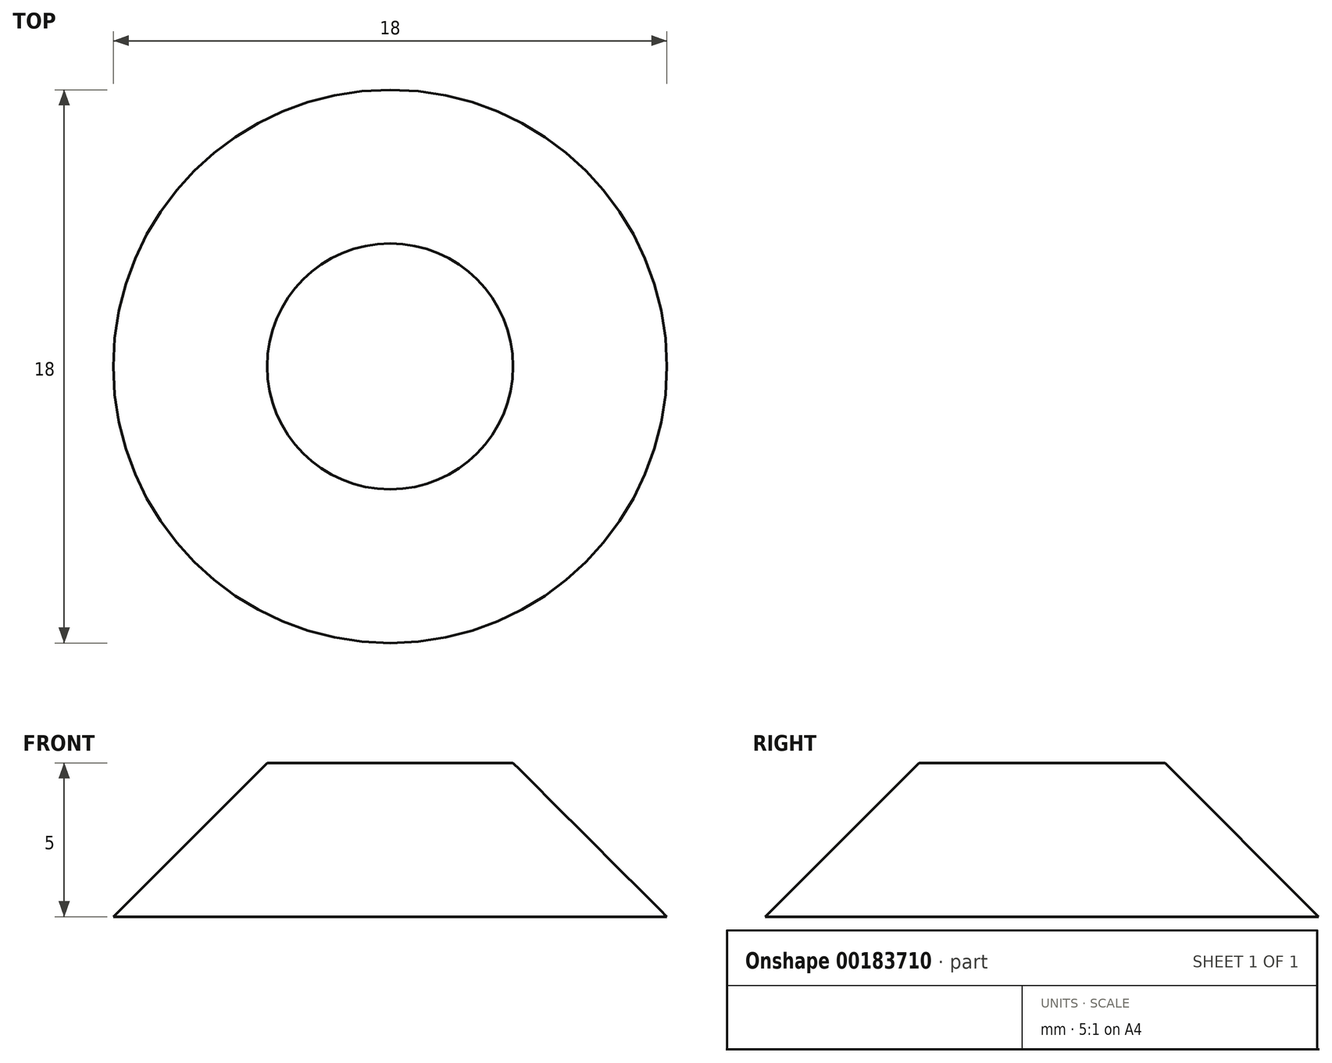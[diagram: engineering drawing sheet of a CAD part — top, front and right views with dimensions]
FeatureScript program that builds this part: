
annotation { "Feature Type Name" : "Feature", "Feature Type Description" : "" }
export const myFeature = defineFeature(function(context is Context, id is Id, definition is map)
    precondition{}
    {
        {
            var Q0;
            Q0=qCreatedBy(makeId("Front.planeOp"),FACE);
            var sketch = newSketch(context, id + "F0", { "sketchPlane" : qUnion([Q0])});
            skLineSegment(sketch, "E0", {"start": v(0, 0) * mm, "end": v(0, 54) * mm});
            skLineSegment(sketch, "E1", {"start": v(0, 37) * mm, "end": v(17, 37) * mm});
            skLineSegment(sketch, "E2", {"start": v(17, 37) * mm, "end": v(-17, 37) * mm});
            skLineSegment(sketch, "E3", {"start": v(0, 54) * mm, "end": v(-17, 37) * mm});
            skLineSegment(sketch, "E4", {"start": v(-17, 37) * mm, "end": v(0, 0) * mm});
            skLineSegment(sketch, "E5", {"start": v(0, 0) * mm, "end": v(17, 37) * mm});
            skLineSegment(sketch, "E6", {"start": v(17, 37) * mm, "end": v(0, 54) * mm});
            skSolve(sketch);
        }
        {
            var Q0;
            Q0=qCreatedBy(makeId("Right.planeOp"),FACE);
            var sketch = newSketch(context, id + "F1", { "sketchPlane" : qUnion([Q0])});
            skLineSegment(sketch, "E7", {"start": v(0, 0) * mm, "end": v(0, 37) * mm});
            skLineSegment(sketch, "E8", {"start": v(0, 37) * mm, "end": v(-10, 37) * mm});
            skLineSegment(sketch, "E9", {"start": v(0, 37) * mm, "end": v(10, 37) * mm});
            skLineSegment(sketch, "E10", {"start": v(0, 54.14) * mm, "end": v(10, 37) * mm});
            skLineSegment(sketch, "E11", {"start": v(0, 54.14) * mm, "end": v(-10, 37) * mm});
            skLineSegment(sketch, "E12", {"start": v(-10, 37) * mm, "end": v(0, 0) * mm});
            skLineSegment(sketch, "E13", {"start": v(10, 37) * mm, "end": v(0, 0) * mm});
            skSolve(sketch);
        }
        {
            var Q0;
            Q0=qCreatedBy(makeId("Top.planeOp"),FACE);
            var sketch = newSketch(context, id + "F2", { "sketchPlane" : qUnion([Q0])});
            skCircle(sketch, "E14", {"center": v(0, 0) * mm, "radius": 9 * mm});
            skSolve(sketch);
        }
        {
            var Q0;
            Q0=makeQuery(id+"F2.imprint","IMPRINT",FACE,{"disambiguationData":[TD([[makeQuery(id+"F2.imprint","IMPRINT",EDGE,{"derivedFrom":sQuery(id+"F2.wireOp",EDGE,"E14")}),1.0]])]});
            extrude(context, id + "F3", {"entities" : qUnion([Q0]), "depth" : 5 * mm});
        }
        {
            var Q0;
            Q0=makeQuery(id+"F3.opExtrude","CAP_FACE",FACE,{"disambiguationData":[OSD([sQuery(id+"F2.wireOp",EDGE,"E14")])],"isStart":false});
            chamfer(context, id + "F4", {"entities" : qUnion([Q0]), "width" : 5 * mm, "tangentPropagation" : true});
        }
        {
            var Q0;
            Q0=sQuery(id+"F0.wireOp",EDGE,"E6");
            var Q1;
            Q1=sQuery(id+"F1.wireOp",EDGE,"E11");
            loft(context, id + "F5", {"bodyType" : ToolBodyType.SURFACE, "wireProfilesArray" : [{ "wireProfileEntities" : qUnion([Q0]) }, { "wireProfileEntities" : qUnion([Q1]) }]});
        }
        {
            var Q0;
            Q0=sQuery(id+"F0.wireOp",EDGE,"E6");
            var Q1;
            Q1=sQuery(id+"F1.wireOp",EDGE,"E10");
            loft(context, id + "F6", {"bodyType" : ToolBodyType.SURFACE, "wireProfilesArray" : [{ "wireProfileEntities" : qUnion([Q0]) }, { "wireProfileEntities" : qUnion([Q1]) }]});
        }
        {
            var Q0;
            Q0=sQuery(id+"F1.wireOp",EDGE,"E11");
            var Q1;
            Q1=sQuery(id+"F0.wireOp",EDGE,"E3");
            loft(context, id + "F7", {"bodyType" : ToolBodyType.SURFACE, "wireProfilesArray" : [{ "wireProfileEntities" : qUnion([Q0]) }, { "wireProfileEntities" : qUnion([Q1]) }]});
        }
        {
            var Q0;
            Q0=sQuery(id+"F1.wireOp",EDGE,"E10");
            var Q1;
            Q1=sQuery(id+"F0.wireOp",EDGE,"E3");
            loft(context, id + "F8", {"bodyType" : ToolBodyType.SURFACE, "wireProfilesArray" : [{ "wireProfileEntities" : qUnion([Q0]) }, { "wireProfileEntities" : qUnion([Q1]) }]});
        }
        {
            var Q0;
            Q0=sQuery(id+"F1.wireOp",EDGE,"E13");
            var Q1;
            Q1=sQuery(id+"F0.wireOp",EDGE,"E4");
            loft(context, id + "F9", {"bodyType" : ToolBodyType.SURFACE, "wireProfilesArray" : [{ "wireProfileEntities" : qUnion([Q0]) }, { "wireProfileEntities" : qUnion([Q1]) }]});
        }
        {
            var Q0;
            Q0=makeQuery(id+"F1.imprint","IMPRINT",FACE,{"disambiguationData":[TD([[makeQuery(id+"F1.imprint","IMPRINT",EDGE,{"derivedFrom":sQuery(id+"F1.wireOp",EDGE,"E7")}),-1.0]])]});
            var Q1;
            {var subQ0=sQuery(id+"F0.wireOp",EDGE,"E5");Q1=makeQuery(id+"F0.imprint","IMPRINT",FACE,{"disambiguationData":[TD([[makeQuery(id+"F0.imprint","IMPRINT",EDGE,{"derivedFrom":subQ0}),1.0]])]});}
            var Q2;
            Q2=sQuery(id+"F0.wireOp",EDGE,"E4");
            var Q3;
            Q3=sQuery(id+"F1.wireOp",EDGE,"E13");
            loft(context, id + "F10", {"bodyType" : ToolBodyType.SURFACE, "sheetProfilesArray" : [{ "sheetProfileEntities" : qUnion([Q0]) }, { "sheetProfileEntities" : qUnion([Q1]) }], "wireProfilesArray" : [{ "wireProfileEntities" : qUnion([Q2]) }, { "wireProfileEntities" : qUnion([Q3]) }]});
        }
        {
            var Q0;
            Q0=sQuery(id+"F0.wireOp",EDGE,"E5");
            var Q1;
            Q1=sQuery(id+"F1.wireOp",EDGE,"E13");
            loft(context, id + "F11", {"bodyType" : ToolBodyType.SURFACE, "wireProfilesArray" : [{ "wireProfileEntities" : qUnion([Q0]) }, { "wireProfileEntities" : qUnion([Q1]) }]});
        }
        {
            var Q0;
            Q0=sQuery(id+"F1.wireOp",EDGE,"E12");
            var Q1;
            Q1=sQuery(id+"F1.wireOp",EDGE,"E7");
            loft(context, id + "F12", {"bodyType" : ToolBodyType.SURFACE, "wireProfilesArray" : [{ "wireProfileEntities" : qUnion([Q0]) }, { "wireProfileEntities" : qUnion([Q1]) }]});
        }
        {
            var Q0;
            Q0=sQuery(id+"F1.wireOp",EDGE,"E7");
            var Q1;
            Q1=sQuery(id+"F0.wireOp",EDGE,"E4");
            loft(context, id + "F13", {"bodyType" : ToolBodyType.SURFACE, "wireProfilesArray" : [{ "wireProfileEntities" : qUnion([Q0]) }, { "wireProfileEntities" : qUnion([Q1]) }]});
        }
        {
            var Q0;
            Q0=makeQuery(id+"F7.opLoft","SWEPT_EDGE",EDGE,{"disambiguationData":[OSD([sQuery(id+"F0.wireOp",VERTEX,"E3.end"),sQuery(id+"F1.wireOp",VERTEX,"E11.end")])]});
            var Q1;
            Q1=sQuery(id+"F0.wireOp",EDGE,"E2");
            loft(context, id + "F14", {"bodyType" : ToolBodyType.SURFACE, "wireProfilesArray" : [{ "wireProfileEntities" : qUnion([Q0]) }, { "wireProfileEntities" : qUnion([Q1]) }]});
        }
        {
            var Q0;
            Q0=makeQuery(id+"F13.opLoft","SWEPT_BODY",BODY,{"disambiguationData":[OSD([sQuery(id+"F0.wireOp",EDGE,"E4"),sQuery(id+"F1.wireOp",EDGE,"E7")])]});
            var Q1;
            Q1=qCreatedBy(makeId("Right.planeOp"),FACE);
            mirror(context, id + "F15", {"entities" : qUnion([Q0]), "mirrorPlane" : qUnion([Q1])});
        }
        {
            var Q0;
            Q0=makeQuery(id+"F12.opLoft","MID_CAP_EDGE",EDGE,{"disambiguationData":[OSD([sQuery(id+"F1.wireOp",VERTEX,"E12.start"),sQuery(id+"F1.wireOp",VERTEX,"E12.end"),sQuery(id+"F1.wireOp",EDGE,"E12")])],"capPos":0.0});
            var Q1;
            Q1=makeQuery(id+"F9.opLoft","MID_CAP_EDGE",EDGE,{"disambiguationData":[OSD([sQuery(id+"F0.wireOp",VERTEX,"E4.start"),sQuery(id+"F0.wireOp",VERTEX,"E4.end"),sQuery(id+"F0.wireOp",EDGE,"E4")])],"capPos":1.0});
            loft(context, id + "F16", {"bodyType" : ToolBodyType.SURFACE, "wireProfilesArray" : [{ "wireProfileEntities" : qUnion([Q0]) }, { "wireProfileEntities" : qUnion([Q1]) }]});
        }
    });
